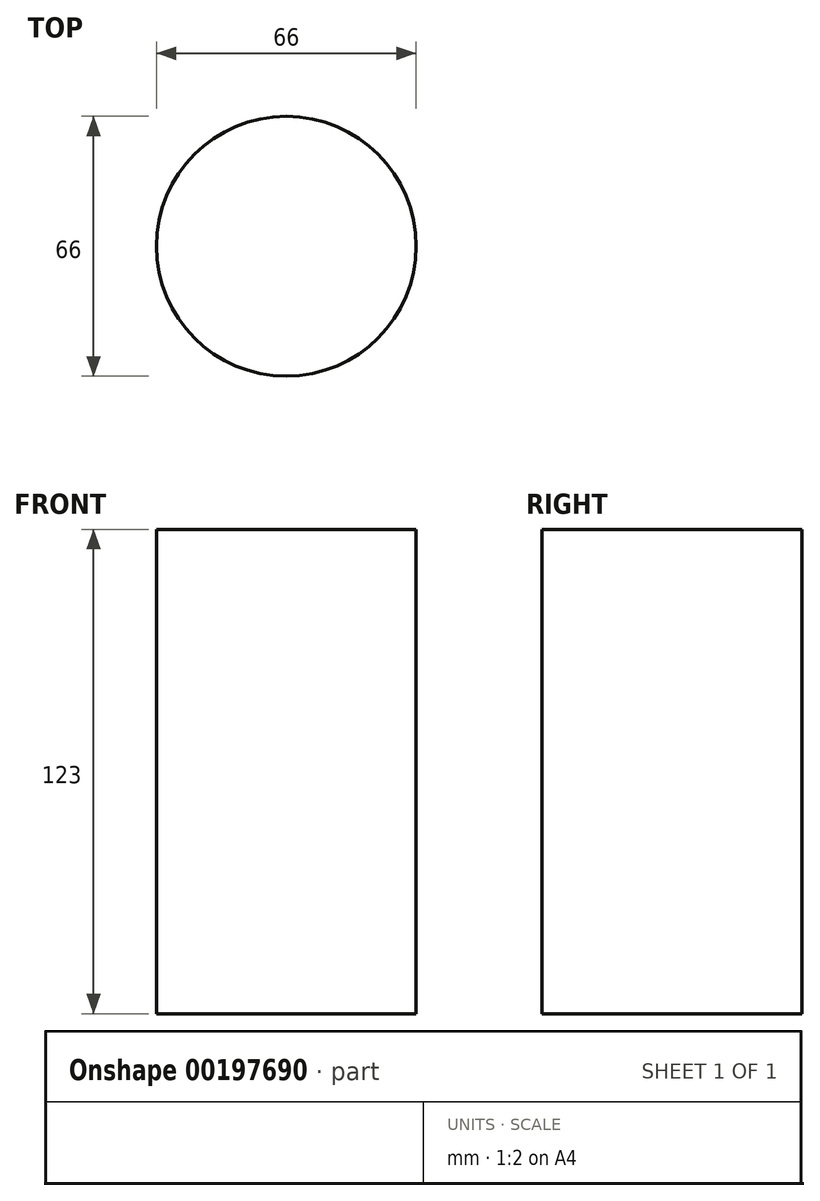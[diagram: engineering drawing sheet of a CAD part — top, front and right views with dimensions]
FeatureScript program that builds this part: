
annotation { "Feature Type Name" : "Feature", "Feature Type Description" : "" }
export const myFeature = defineFeature(function(context is Context, id is Id, definition is map)
    precondition{}
    {
        {
            var Q0;
            Q0=qCreatedBy(makeId("Top.planeOp"),FACE);
            var sketch = newSketch(context, id + "F0", { "sketchPlane" : qUnion([Q0])});
            skCircle(sketch, "E0", {"center": v(-34.6, 15.18) * mm, "radius": 33 * mm});
            skSolve(sketch);
        }
        {
            var Q0;
            Q0=makeQuery(id+"F0.imprint","IMPRINT",FACE,{"disambiguationData":[TD([[makeQuery(id+"F0.imprint","IMPRINT",EDGE,{"derivedFrom":sQuery(id+"F0.wireOp",EDGE,"E0")}),1.0]])]});
            extrude(context, id + "F1", {"entities" : qUnion([Q0]), "depth" : 123 * mm});
        }
    });
